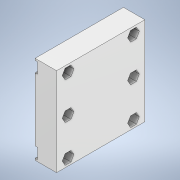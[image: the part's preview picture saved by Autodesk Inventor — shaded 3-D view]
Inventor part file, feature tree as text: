
AUTODESK INVENTOR PART (.ipt)
format: ipt  version: 2020 (Build 240168000, 168)  size: 199,680 bytes
history: native  units: mm
features: extrude x4, sketch x3, other x1
ambient origin geometry x8: Origin, YZ Plane, XZ Plane, XY Plane, X Axis, Y Axis, Z Axis, Center Point
bodies: Body1 (feature_tree)
feature tree (8):
  other  "Bryła1"
  extrude  "Wyciągnięcie proste1"  Depth=74.0mm
  sketch  "Szkic2"
  extrude  "Wyciągnięcie proste2"  Depth=74.0mm
  extrude  "Wyciągnięcie proste3"  Depth=18.0mm TaperAngle=0.0deg
  extrude  "Wyciągnięcie proste4"  Depth=6.0mm
  sketch  "Szkic1"
  sketch  "Szkic3"
